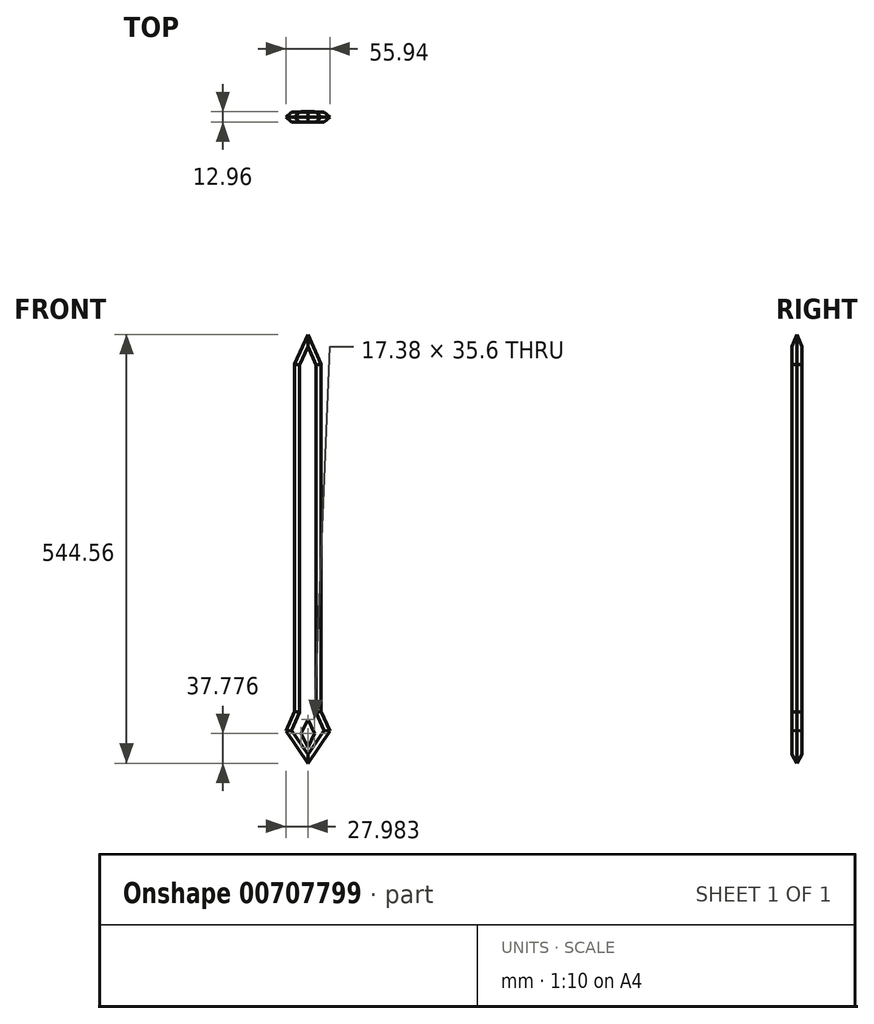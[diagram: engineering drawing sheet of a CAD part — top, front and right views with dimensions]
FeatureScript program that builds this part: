
annotation { "Feature Type Name" : "Feature", "Feature Type Description" : "" }
export const myFeature = defineFeature(function(context is Context, id is Id, definition is map)
    precondition{}
    {
        {
            var Q0;
            Q0=qCreatedBy(makeId("Front.planeOp"),FACE);
            var sketch = newSketch(context, id + "F0", { "sketchPlane" : qUnion([Q0])});
            skLineSegment(sketch, "E0", {"start": v(-27.98, 3.42) * mm, "end": v(0, -37.77) * mm});
            skLineSegment(sketch, "E1", {"start": v(0, -37.77) * mm, "end": v(27.96, 3.42) * mm});
            skLineSegment(sketch, "E2", {"start": v(-27.98, 3.42) * mm, "end": v(-17.14, 28.2) * mm});
            skLineSegment(sketch, "E3", {"start": v(27.96, 3.42) * mm, "end": v(17.08, 28.2) * mm});
            skLineSegment(sketch, "E4", {"start": v(17.08, 28.2) * mm, "end": v(27.96, 3.42) * mm});
            skLineSegment(sketch, "E5", {"start": v(-17.14, 28.2) * mm, "end": v(-17.14, 469.12) * mm});
            skLineSegment(sketch, "E6", {"start": v(-17.14, 469.12) * mm, "end": v(-17.14, 28.2) * mm});
            skLineSegment(sketch, "E7", {"start": v(17.08, 28.2) * mm, "end": v(17.08, 469.12) * mm});
            skLineSegment(sketch, "E8", {"start": v(-17.14, 469.12) * mm, "end": v(0, 506.79) * mm});
            skLineSegment(sketch, "E9", {"start": v(0, 506.79) * mm, "end": v(17.08, 469.12) * mm});
            skSolve(sketch);
        }
        {
            var Q0;
            Q0=makeQuery(id+"F0.imprint","IMPRINT",FACE,{"disambiguationData":[TD([[makeQuery(id+"F0.imprint","IMPRINT",EDGE,{"derivedFrom":sQuery(id+"F0.wireOp",EDGE,"E0")}),1.0]])]});
            extrude(context, id + "F1", {"entities" : qUnion([Q0]), "depth" : 6.35 * mm, "offsetDistance" : 25.4 * mm});
        }
        {
            var Q0;
            Q0=makeQuery(id+"F1.opExtrude","CAP_FACE",FACE,{"disambiguationData":[OSD([sQuery(id+"F0.wireOp",EDGE,"E0"),sQuery(id+"F0.wireOp",EDGE,"E1"),sQuery(id+"F0.wireOp",EDGE,"E2"),sQuery(id+"F0.wireOp",EDGE,"E4"),sQuery(id+"F0.wireOp",EDGE,"E6"),sQuery(id+"F0.wireOp",EDGE,"E7"),sQuery(id+"F0.wireOp",EDGE,"E8"),sQuery(id+"F0.wireOp",EDGE,"E9")])],"isStart":true});
            extrude(context, id + "F2", {"entities" : qUnion([Q0]), "operationType" : NewBodyOperationType.ADD, "depth" : 6.35 * mm, "offsetDistance" : 25.4 * mm});
        }
        {
            var Q0;
            Q0=makeQuery(id+"F1.opExtrude","CAP_FACE",FACE,{"disambiguationData":[OSD([sQuery(id+"F0.wireOp",EDGE,"E0"),sQuery(id+"F0.wireOp",EDGE,"E1"),sQuery(id+"F0.wireOp",EDGE,"E2"),sQuery(id+"F0.wireOp",EDGE,"E4"),sQuery(id+"F0.wireOp",EDGE,"E6"),sQuery(id+"F0.wireOp",EDGE,"E7"),sQuery(id+"F0.wireOp",EDGE,"E8"),sQuery(id+"F0.wireOp",EDGE,"E9")])],"isStart":false});
            var Q1;
            Q1=makeQuery(id+"F2.opExtrude","CAP_FACE",FACE,{"disambiguationData":[OSD([sQuery(id+"F0.wireOp",EDGE,"E0"),sQuery(id+"F0.wireOp",EDGE,"E1"),sQuery(id+"F0.wireOp",EDGE,"E2"),sQuery(id+"F0.wireOp",EDGE,"E4"),sQuery(id+"F0.wireOp",EDGE,"E6"),sQuery(id+"F0.wireOp",EDGE,"E7"),sQuery(id+"F0.wireOp",EDGE,"E8"),sQuery(id+"F0.wireOp",EDGE,"E9")])],"isStart":false});
            chamfer(context, id + "F3", {"entities" : qUnion([Q0, Q1]), "chamferType" : ChamferType.OFFSET_ANGLE, "width" : 6.35 * mm, "oppositeDirection" : false, "angle" : 45 * degree, "tangentPropagation" : true});
        }
        {
            var Q0;
            Q0=makeQuery(id+"F1.opExtrude","CAP_FACE",FACE,{"disambiguationData":[OSD([sQuery(id+"F0.wireOp",EDGE,"E0"),sQuery(id+"F0.wireOp",EDGE,"E1"),sQuery(id+"F0.wireOp",EDGE,"E2"),sQuery(id+"F0.wireOp",EDGE,"E4"),sQuery(id+"F0.wireOp",EDGE,"E6"),sQuery(id+"F0.wireOp",EDGE,"E7"),sQuery(id+"F0.wireOp",EDGE,"E8"),sQuery(id+"F0.wireOp",EDGE,"E9")])],"isStart":false});
            extrude(context, id + "F4", {"entities" : qUnion([Q0]), "operationType" : NewBodyOperationType.REMOVE, "oppositeDirection" : true, "depth" : 0.13 * mm, "offsetDistance" : 25.4 * mm});
        }
        {
            var Q0;
            Q0=makeQuery(id+"F2.opExtrude","CAP_FACE",FACE,{"disambiguationData":[OSD([sQuery(id+"F0.wireOp",EDGE,"E0"),sQuery(id+"F0.wireOp",EDGE,"E1"),sQuery(id+"F0.wireOp",EDGE,"E2"),sQuery(id+"F0.wireOp",EDGE,"E4"),sQuery(id+"F0.wireOp",EDGE,"E6"),sQuery(id+"F0.wireOp",EDGE,"E7"),sQuery(id+"F0.wireOp",EDGE,"E8"),sQuery(id+"F0.wireOp",EDGE,"E9")])],"isStart":false});
            extrude(context, id + "F5", {"entities" : qUnion([Q0]), "operationType" : NewBodyOperationType.REMOVE, "oppositeDirection" : true, "depth" : 0.13 * mm, "offsetDistance" : 25.4 * mm});
        }
        {
            var Q0;
            Q0=makeQuery(id+"F4.boolean.opBoolean","COPY",FACE,{"derivedFrom":makeQuery(id+"F4.opExtrude","CAP_FACE",FACE,{"disambiguationData":[OSD([sQuery(id+"F0.wireOp",EDGE,"E0"),sQuery(id+"F0.wireOp",EDGE,"E1"),sQuery(id+"F0.wireOp",EDGE,"E2"),sQuery(id+"F0.wireOp",EDGE,"E4"),sQuery(id+"F0.wireOp",EDGE,"E6"),sQuery(id+"F0.wireOp",EDGE,"E7"),sQuery(id+"F0.wireOp",EDGE,"E8"),sQuery(id+"F0.wireOp",EDGE,"E9")])],"isStart":false})});
            var sketch = newSketch(context, id + "F6", { "sketchPlane" : qUnion([Q0])});
            skLineSegment(sketch, "E10", {"start": v(0, 17.8) * mm, "end": v(-8.69, 0) * mm});
            skLineSegment(sketch, "E11", {"start": v(-8.69, 0) * mm, "end": v(0, -17.8) * mm});
            skLineSegment(sketch, "E12", {"start": v(0, -17.8) * mm, "end": v(8.7, 0) * mm});
            skLineSegment(sketch, "E13", {"start": v(8.7, 0) * mm, "end": v(0, 17.8) * mm});
            skSolve(sketch);
        }
        {
            var Q0;
            Q0=makeQuery(id+"F6.imprint","IMPRINT",FACE,{"disambiguationData":[TD([[makeQuery(id+"F6.imprint","IMPRINT",EDGE,{"derivedFrom":sQuery(id+"F6.wireOp",EDGE,"E10")}),1.0]])]});
            extrude(context, id + "F7", {"entities" : qUnion([Q0]), "operationType" : NewBodyOperationType.ADD, "depth" : 0.25 * mm, "offsetDistance" : 25.4 * mm});
        }
        {
            var Q0;
            Q0=makeQuery(id+"F7.opExtrude","CAP_FACE",FACE,{"disambiguationData":[OSD([sQuery(id+"F6.wireOp",EDGE,"E10"),sQuery(id+"F6.wireOp",EDGE,"E11"),sQuery(id+"F6.wireOp",EDGE,"E12"),sQuery(id+"F6.wireOp",EDGE,"E13")])],"isStart":false});
            extrude(context, id + "F8", {"entities" : qUnion([Q0]), "operationType" : NewBodyOperationType.ADD, "oppositeDirection" : true, "depth" : 12.95 * mm, "offsetDistance" : 25.4 * mm});
        }
    });
